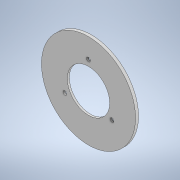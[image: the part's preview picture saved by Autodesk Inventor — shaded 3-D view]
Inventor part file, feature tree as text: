
AUTODESK INVENTOR PART (.ipt)
format: ipt  version: 2020 (Build 240168000, 168)  size: 425,984 bytes
history: native  units: in
note: dims shown in document units (in); Inventor stores cm internally (conversion verified against a paired STEP export)
features: sketch x14, extrude x11, projected_geometry x6, plane x2, shell x1, sweep x1, hole x1
ambient origin geometry x8: Origin, YZ Plane, XZ Plane, XY Plane, X Axis, Y Axis, Z Axis, Center Point
bodies: Solid1 (feature_tree)
feature tree (36):
  extrude  "Extrusion1"  Depth=3.1496in TaperAngle=0.0deg
  shell  "Shell1"  Thickness=0.1181in
  extrude  "Extrusion2"  Depth=3.1496in TaperAngle=0.0deg
  extrude  "Extrusion3"  Depth=1.5748in
  plane  "Work Plane1"
  extrude  "Extrusion4"  TaperAngle=120.0deg  [1 undecoded]
  extrude  "Extrusion5"  Depth=0.378in
  plane  "Work Plane4"
  sweep  "Sweep2"
  extrude  "Extrusion6"  [1 undecoded]
  hole  "Hole1"  [1 undecoded]
  extrude  "Extrusion9"  Depth=0.1181in TaperAngle=0.0deg
  extrude  "Extrusion10"  Depth=0.0591in
  extrude  "Extrusion11"  Depth=0.0591in
  extrude  "Extrusion13"  Depth=0.0591in
  extrude  "Extrusion12"  Depth=0.0591in
  sketch  "Sketch1"  dims[d1=5.3543in d2=3.1496in d3=0.0in d4=0.1181in]
  sketch  "Sketch2"  dims[d5=2.5197in d6=3.1496in d7=0.0in]
  sketch  "Sketch3"  dims[d8=0.378in d9=1.5748in]
  projected_geometry  "Projected Loop1"
  sketch  "Sketch4"  dims[d10=120.0deg d11=120.0deg]
  sketch  "Sketch6"  dims[d12=0.378in d13=0.378in]
  projected_geometry  "Projected Loop3"
  sketch  "Sketch9"  dims[d14=1.5748in d15=1.5748in]
  projected_geometry  "Projected Loop4"
  sketch  "Sketch10"  dims[d16=0.06in d17=0.0in d18=-0.9843in]
  sketch  "Sketch11"  dims[d24=1.1811in d25=0.9843in d26=0.0in]
  projected_geometry  "Projected Loop5"
  sketch  "Sketch14"  dims[d27=0.1181in d28=2.2201in d29=0.0in]
  sketch  "Sketch16"  dims[d37=0.0in d38=0.0in d39=0.0591in]
  sketch  "Sketch17"  dims[d40=0.0591in d41=0.0591in]
  projected_geometry  "Projected Loop7"
  sketch  "Sketch18"  dims[d42=0.0591in d43=0.0591in]
  sketch  "Sketch19"  dims[d44=0.0591in d45=0.0591in]
  sketch  "Sketch20"  dims[d46=0.9843in d47=0.9843in d48=0.9843in d49=0.9843in d50=0.9843in d51=0.9843in d52=0.0591in d53=0.0in d98=0.2362in d99=1.6142in d100=1.1811in d102=360.0deg d104=0.2362in d105=0.2362in d106=0.1575in d107=0.0787in d108=90.0deg d109=0.315in d110=0.8108in d111=0.3937in d112=0.0in d113=0.3937in d114=0.0in d115=5.5906in d116=0.378in d117=5.1181in d118=2.2638in d119=0.0591in d120=0.7874in d121=0.7874in d122=2.3622in d124=360.0deg d126=0.0591in d127=0.0591in d128=2.3622in d130=360.0deg d132=0.0591in d133=0.0in d134=0.378in d135=2.2638in d136=2.3622in d138=360.0deg d140=0.06in d141=0.0in d142=0.0591in d143=0.0in]
  projected_geometry  "Projected Loop8"
note: 3 required parameter values undecoded (feature->parameter linkage not recoverable at this tier; creation-order binding heuristic only, values carry confidence <= 0.55)
